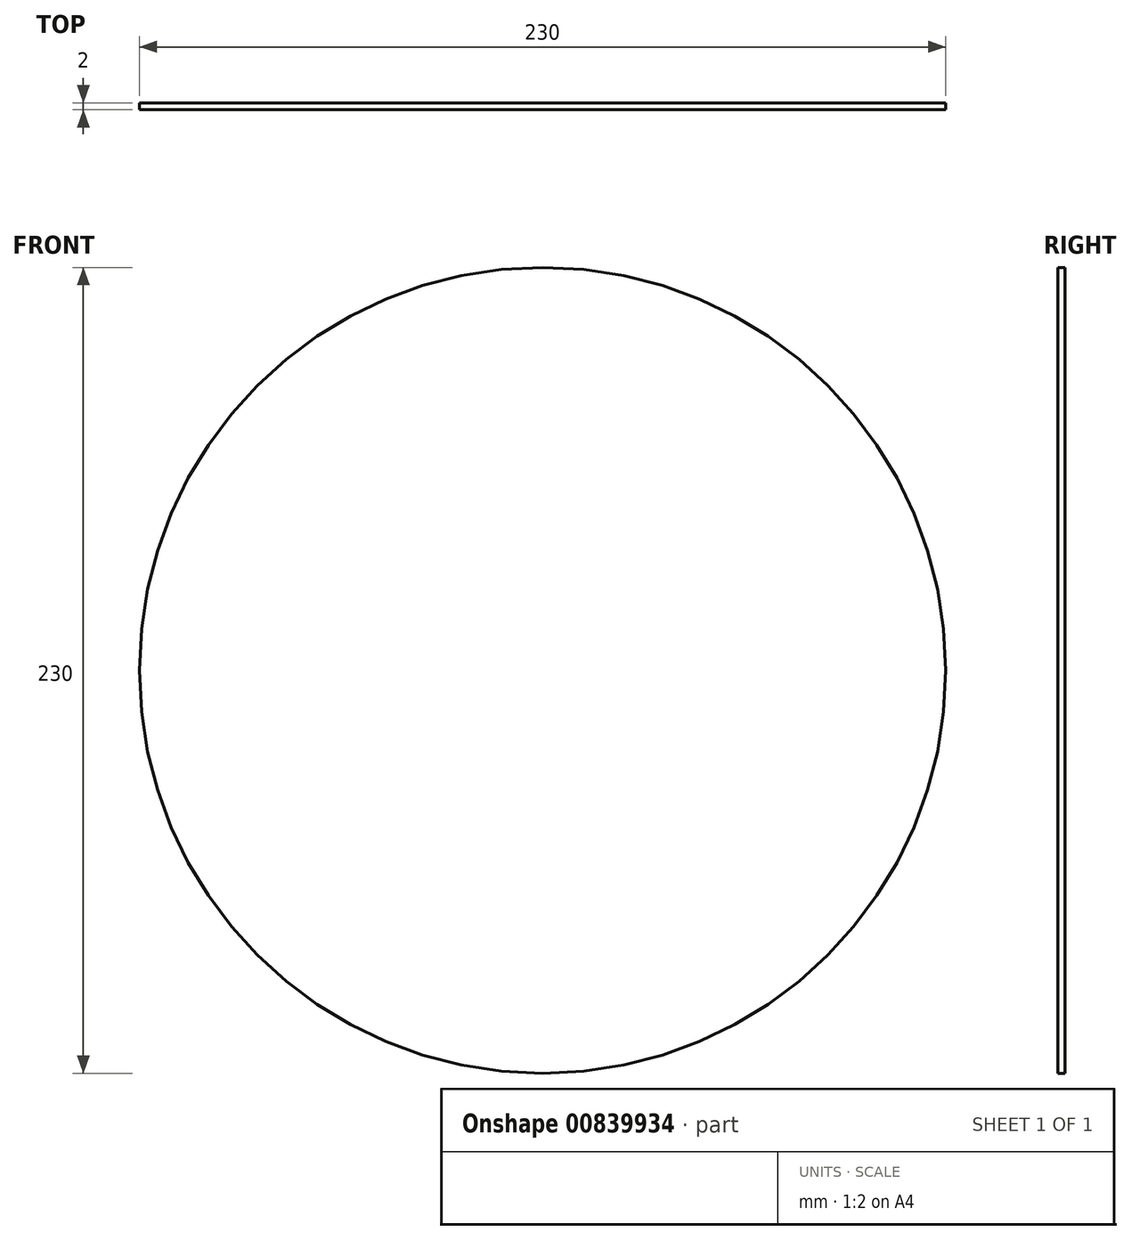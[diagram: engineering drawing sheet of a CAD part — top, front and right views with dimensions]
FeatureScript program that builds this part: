
annotation { "Feature Type Name" : "Feature", "Feature Type Description" : "" }
export const myFeature = defineFeature(function(context is Context, id is Id, definition is map)
    precondition{}
    {
        {
            var Q0;
            Q0=qCreatedBy(makeId("Front.planeOp"),FACE);
            var sketch = newSketch(context, id + "F0", { "sketchPlane" : qUnion([Q0])});
            skCircle(sketch, "E0", {"center": v(0, 0) * mm, "radius": 115 * mm});
            skSolve(sketch);
        }
        {
            var Q0;
            Q0=makeQuery(id+"F0.imprint","IMPRINT",FACE,{"disambiguationData":[TD([[makeQuery(id+"F0.imprint","IMPRINT",EDGE,{"derivedFrom":sQuery(id+"F0.wireOp",EDGE,"E0")}),1.0]])]});
            var Q1;
            Q1=sQuery(id+"F0.wireOp",EDGE,"E0");
            extrude(context, id + "F1", {"entities" : qUnion([Q0]), "surfaceEntities" : qUnion([Q1]), "oppositeDirection" : true, "depth" : 2 * mm, "offsetDistance" : 25 * mm});
        }
    });
